# Revit family: Sink-Top_Mount-Kohler-Langlade-6626X
name_source: partatom
category: Plumbing Fixtures
revit_build: Autodesk Revit MEP 2012 (Build: 20110916_2132(x64)
units: mm (PartAtom-declared; Revit-internal decimal feet)

## types (11) — shared parameters
Date Modified = March 13, 2015
Depth = 22 "
Description = See Part Description
Drain Flow = 0 GPM
Drain Radius = 0.625 "
Equipment Abbreviation = LDS
Family Version = 1.0
Height = 9.625 "
Manufacturer = Kohler Company
Model = See Part Number
Model Disclaimer = Contact Kohler Company For More Information
Product Page URL = http://www.us.kohler.com
URL = http://www.us.kohler.com
Width = 33 "
zz Length 10 = 30.56 "
zz Length 2 = 9.625 "
zz Length 3 = 33 "
zz Length 5 = 22 "

## per-type parameters (varying)
| type | Product Material | zz Integer 2 |
| White | Cast Iron - Kohler - White Enamel | 1 |
| Sea Salt | Cast Iron - Kohler - Sea Salt Enamel | 5 |
| Biscuit | Cast Iron - Kohler - Biscuit Enamel | 2 |
| Almond | Cast Iron - Kohler - Almond Enamel | 3 |
| Cane Sugar | Cast Iron - Kohler - Cane Sugar Enamel | 6 |
| Ice Grey | Cast Iron - Kohler - Ice Grey Enamel | 8 |
| Sandbar | Cast Iron - Kohler - Sandbar Enamel | 9 |
| Cashmere | Cast Iron - Kohler - Cashmere Enamel | 11 |
| Suede | Cast Iron - Kohler - Suede Enamel | 14 |
| Black n Tan | Cast Iron - Kohler - Black n Tan Enamel | 15 |
| Black | Cast Iron - Kohler - Black Enamel | 4 |

## geometry (parser evidence)
native form markers: Blend x16, Sweep x1
no freeform markers — native parametric forms only
